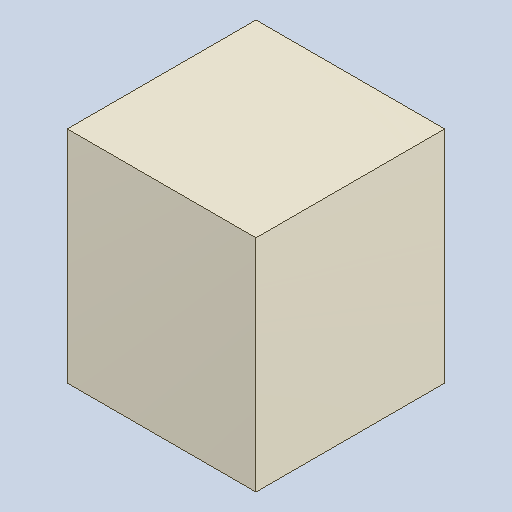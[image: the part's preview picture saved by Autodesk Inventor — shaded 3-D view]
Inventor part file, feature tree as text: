
AUTODESK INVENTOR PART (.ipt)
format: ipt  version: 2023.4 (Build 274418000, 418)  size: 82,944 bytes
history: native  units: mm
features: extrude x1
ambient origin geometry x8: Origin, YZ Plane, XZ Plane, XY Plane, X Axis, Y Axis, Z Axis, Center Point
bodies: Solid1 (feature_tree)
feature tree (1):
  extrude  "Extruded_17"  [1 undecoded]
note: 1 required parameter value undecoded (feature->parameter linkage not recoverable at this tier; creation-order binding heuristic only, values carry confidence <= 0.55)
